# Revit family: Window-Treatment_Solar-Shade_SWFcontract_Motorized-Dual
name_source: partatom
category: Specialty Equipment
units: mm (PartAtom-declared; Revit-internal decimal feet)

## family parameters
Always vertical = No
Classification Number = 23.30.60.14.21
Cut with Voids When Loaded = No
Enable Cutting in Views = No
Maintain Annotation Orientation = No
Part Type = Normal
Room Calculation Point = No
Round Connector Dimension = Use Diameter
Shared = No
Work Plane-Based = Yes

## types (1)
- Window-Treatment_Solar-Shade_SWFcontract_Motorized-Dual
    Assembly Code = E2010320
    Available Options = as Specified
    Blackout Option = No
    Construction Details = http://www.arcat.com
    Default Elevation = 0' - 0"
    Description = SWFcontract Window Treatment as Specified
    Electric Motor = as Specified
    Expected Lifespan (Years) = 0
    Fabric Inset = 0' - 0 9/16"
    Fascia Depth = 0' - 7 1/2"
    Fascia Height = 0' - 8"
    Green Building-LEED = http://www.arcat.com
    Keynote = 12490
    Maintenance Schedule (Months) = 0
    Manufacturer = SWFcontract
    Manufacturer Website = http://www.swfcontract.com
    Model = As Specified
    Pocket Closure = Yes
    Product Data = http://www.arcat.com
    Revision = R1_03-2014
    Sales Information = http://www.swfcontract.com
    Send Message = http://www.arcat.com
    SpecWizard = http://www.arcat.com
    Specification = http://www.arcat.com
    URL = http://www.swfcontract.com
    Unit Height = 6' - 0"
    Unit Width = 2' - 8"
    Warranty Duration (Years) = 0
    With Fascia = No
    Without Fascia = Yes
    controlchainlocate = 0' - 0 1/4"
    fasciadcontrol = 0' - 7 1/2"
    fasciahcontrol = 0' - 8"

## geometry (parser evidence)
native form markers: Blend x3, Sweep x2
no freeform markers — native parametric forms only
